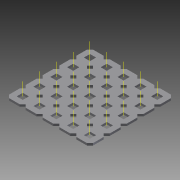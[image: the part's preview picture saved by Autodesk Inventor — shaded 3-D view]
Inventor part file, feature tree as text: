
AUTODESK INVENTOR PART (.ipt)
format: ipt  version: 2015 (Build 190159000, 159)  size: 1,138,688 bytes
history: native  units: in
note: dims shown in document units (in); Inventor stores cm internally (conversion verified against a paired STEP export)
features: other x34, extrude x2, pattern_linear x1, imported_body x1
ambient origin geometry x8: Origin, YZ Plane, XZ Plane, XY Plane, X Axis, Y Axis, Z Axis, Center Point
bodies: Body1 (feature_tree)
feature tree (38):
  other  "Diamond-Pattern"
  other  "Plate"
  extrude  "length cut"  TaperAngle=0.0deg  [1 undecoded]
  extrude  "width cut"  TaperAngle=0.0deg  [1 undecoded]
  other  "constraint axis"
  pattern_linear  "constraint axes"  Spacing1=0.5in  [1 undecoded]
  other  "front plane"
  other  "right plane"
  imported_body  "Base1"
  other  "length profile"
  other  "width profile"
  other  "Work Point1"
  other  "Work Axis36"
  other  "Work Axis40"
  other  "Work Axis41"
  other  "Work Axis42"
  other  "Work Axis43"
  other  "back plane"
  other  "left plane"
  other  "Work Axis120"
  other  "Work Axis121"
  other  "Work Axis122"
  other  "Work Axis123"
  other  "Work Axis170"
  other  "Work Axis171"
  other  "Work Axis172"
  other  "Work Axis173"
  other  "Work Axis174"
  other  "Work Axis175"
  other  "Work Axis176"
  other  "Work Axis177"
  other  "Work Axis178"
  other  "Work Axis179"
  other  "Work Axis180"
  other  "Work Axis181"
  other  "Work Axis182"
  other  "Work Axis183"
  other  "Work Axis184"
note: 3 required parameter values undecoded (feature->parameter linkage not recoverable at this tier; creation-order binding heuristic only, values carry confidence <= 0.55)
